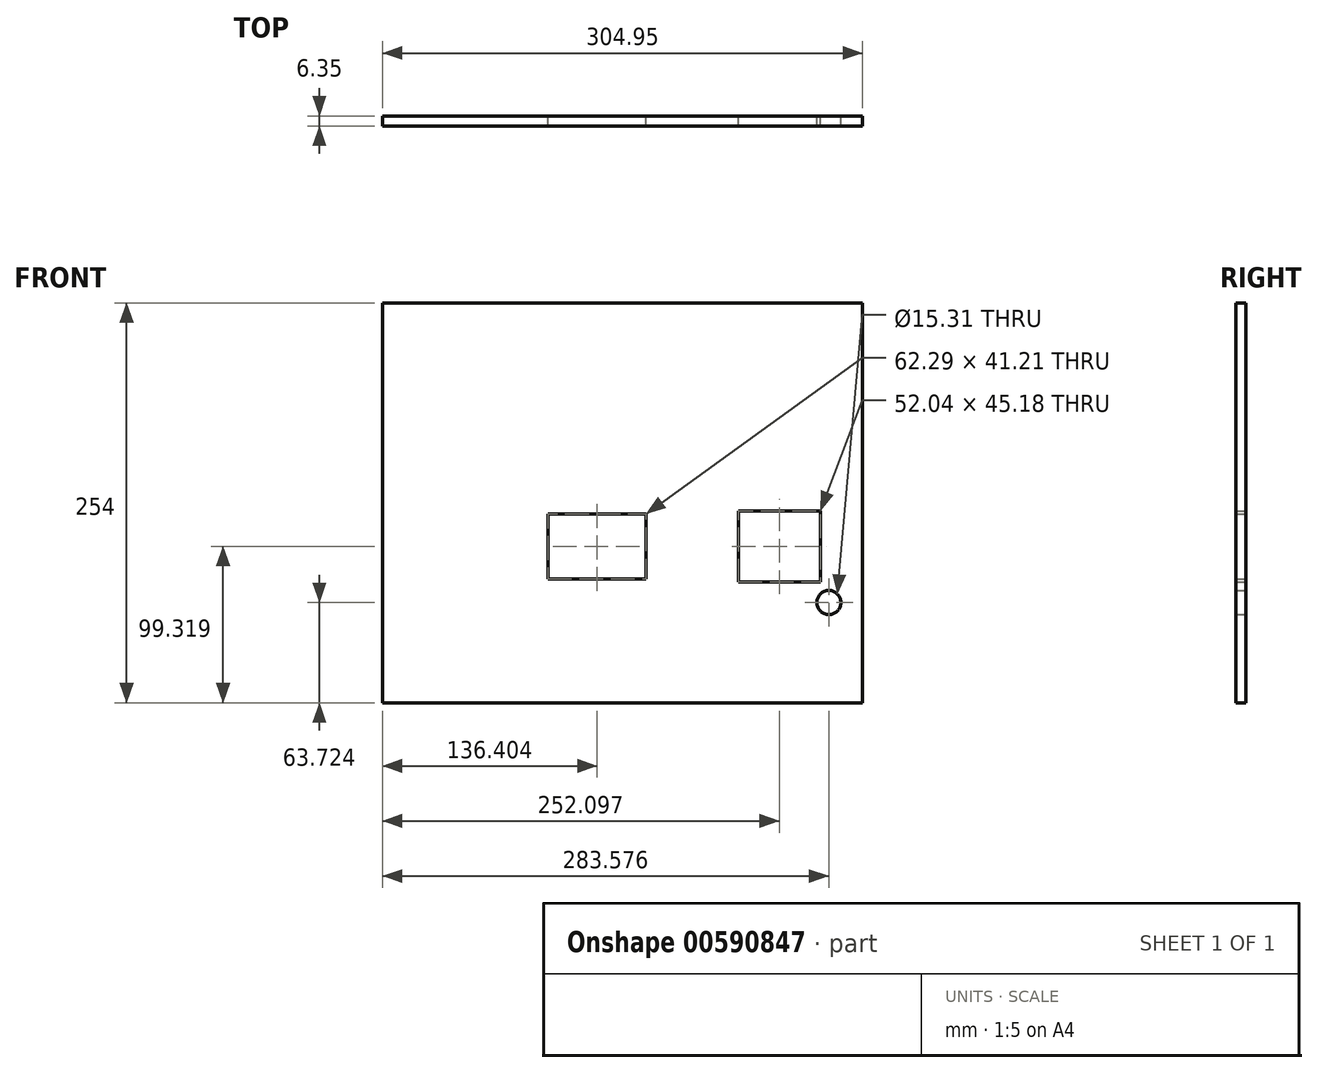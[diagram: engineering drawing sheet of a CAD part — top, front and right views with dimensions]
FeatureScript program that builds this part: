
annotation { "Feature Type Name" : "Feature", "Feature Type Description" : "" }
export const myFeature = defineFeature(function(context is Context, id is Id, definition is map)
    precondition{}
    {
        {
            var Q0;
            Q0=qCreatedBy(makeId("Front.planeOp"),FACE);
            var sketch = newSketch(context, id + "F0", { "sketchPlane" : qUnion([Q0])});
            skLineSegment(sketch, "E0", {"start": v(-153.3, 100) * mm, "end": v(151.5, 100) * mm});
            skLineSegment(sketch, "E1", {"start": v(151.5, 100) * mm, "end": v(151.5, -154) * mm});
            skLineSegment(sketch, "E2", {"start": v(151.5, -154) * mm, "end": v(-153.46, -154) * mm});
            skLineSegment(sketch, "E3", {"start": v(-153.46, -154) * mm, "end": v(-153.46, 43.94) * mm});
            skLineSegment(sketch, "E4", {"start": v(-153.46, 43.94) * mm, "end": v(-153.3, 100) * mm});
            skLineSegment(sketch, "E5", {"start": v(54.13, -154) * mm, "end": v(54.13, 0) * mm});
            skLineSegment(sketch, "E6", {"start": v(54.13, 0) * mm, "end": v(151.5, 0) * mm});
            skLineSegment(sketch, "E7", {"start": v(-48.2, -34.08) * mm, "end": v(14.09, -34.08) * mm});
            skLineSegment(sketch, "E8", {"start": v(14.09, -34.08) * mm, "end": v(14.09, -75.3) * mm});
            skLineSegment(sketch, "E9", {"start": v(14.09, -75.3) * mm, "end": v(-48.2, -75.3) * mm});
            skLineSegment(sketch, "E10", {"start": v(-48.2, -75.3) * mm, "end": v(-48.2, -34.08) * mm});
            skLineSegment(sketch, "E11", {"start": v(72.62, -32.1) * mm, "end": v(72.62, -77.28) * mm});
            skLineSegment(sketch, "E12", {"start": v(72.62, -77.28) * mm, "end": v(124.66, -77.28) * mm});
            skLineSegment(sketch, "E13", {"start": v(124.66, -77.28) * mm, "end": v(124.66, -32.1) * mm});
            skLineSegment(sketch, "E14", {"start": v(124.66, -32.1) * mm, "end": v(72.62, -32.1) * mm});
            skCircle(sketch, "E15", {"center": v(130.12, -90.29) * mm, "radius": 7.65 * mm});
            skSolve(sketch);
        }
        {
            var Q0;
            {var subQ2=sQuery(id+"F0.wireOp",EDGE,"E0");Q0=makeQuery(id+"F0.imprint","IMPRINT",FACE,{"disambiguationData":[TD([[makeQuery(id+"F0.imprint","IMPRINT",EDGE,{"derivedFrom":subQ2}),-1.0]])]});}
            var Q1;
            {var subQ4=sQuery(id+"F0.wireOp",EDGE,"E5");Q1=makeQuery(id+"F0.imprint","IMPRINT",FACE,{"disambiguationData":[TD([[makeQuery(id+"F0.imprint","IMPRINT",EDGE,{"derivedFrom":subQ4}),-1.0]])]});}
            extrude(context, id + "F1", {"entities" : qUnion([Q0, Q1]), "depth" : 6.35 * mm, "offsetDistance" : 25.4 * mm});
        }
    });
